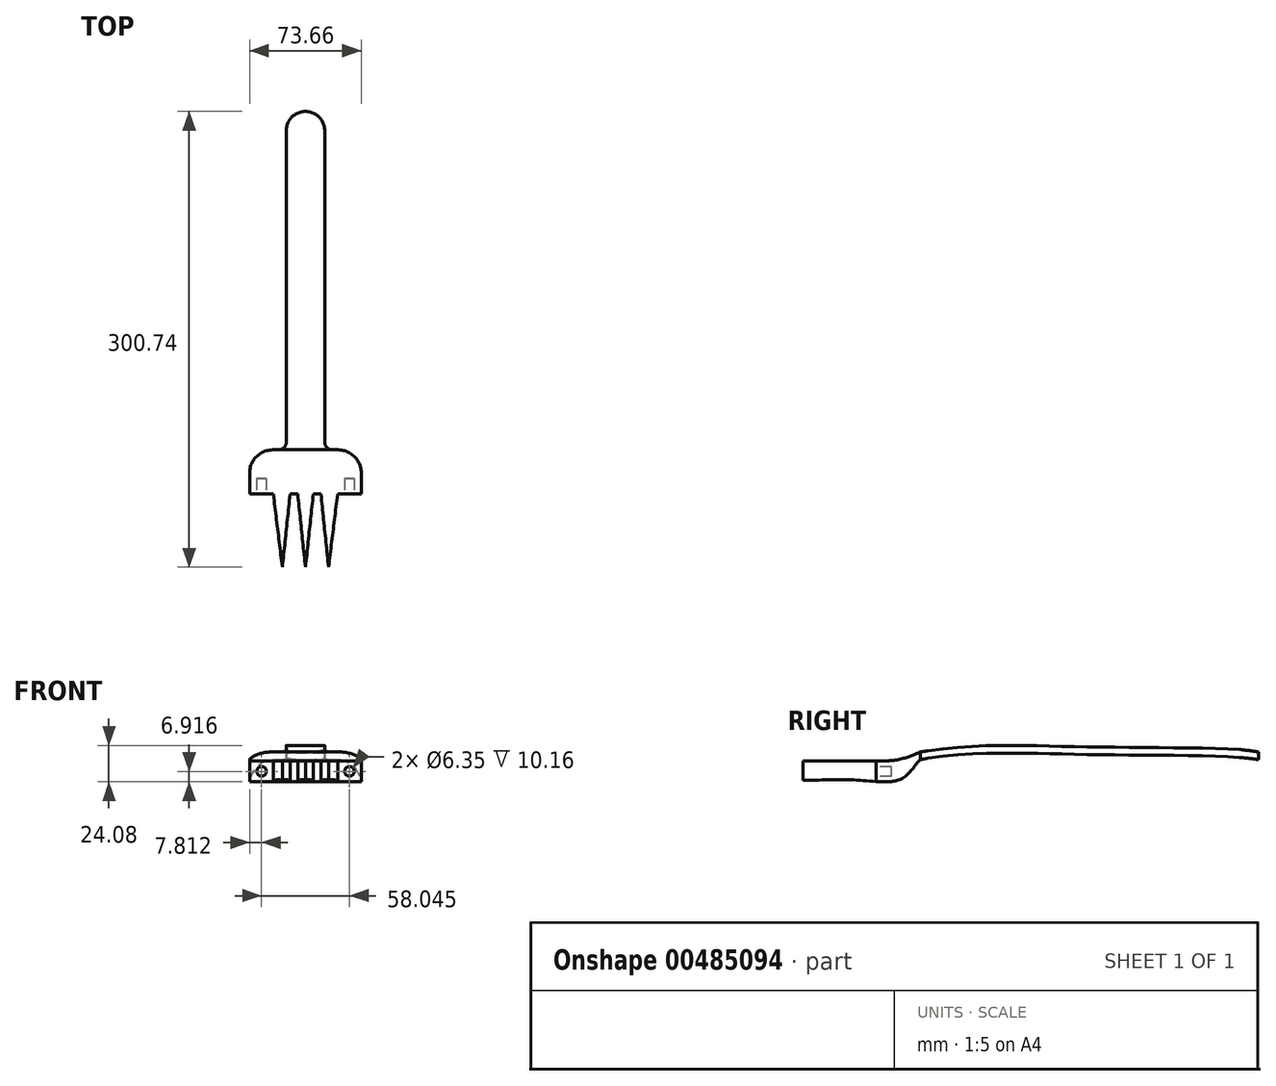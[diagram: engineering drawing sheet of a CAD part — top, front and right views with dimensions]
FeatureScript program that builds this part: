
annotation { "Feature Type Name" : "Feature", "Feature Type Description" : "" }
export const myFeature = defineFeature(function(context is Context, id is Id, definition is map)
    precondition{}
    {
        {
            var Q0;
            Q0=qCreatedBy(makeId("Top.planeOp"),FACE);
            var sketch = newSketch(context, id + "F0", { "sketchPlane" : qUnion([Q0])});
            skLineSegment(sketch, "E0", {"start": v(42, 63.5) * mm, "end": v(42, 0) * mm, "construction": true});
            skPoint(sketch, "E1", {"position": v(26.74, 8.89) * mm});
            skPoint(sketch, "E2", {"position": v(42, 8.89) * mm});
            skLineSegment(sketch, "E3", {"start": v(26.74, 8.89) * mm, "end": v(20.78, 57.15) * mm});
            skLineSegment(sketch, "E4", {"start": v(26.74, 8.89) * mm, "end": v(31.81, 57.15) * mm});
            skLineSegment(sketch, "E5", {"start": v(12.9, 57.15) * mm, "end": v(20.78, 57.15) * mm});
            skLineSegment(sketch, "E6", {"start": v(31.81, 57.15) * mm, "end": v(36.86, 57.15) * mm});
            skLineSegment(sketch, "E7", {"start": v(36.86, 57.15) * mm, "end": v(42, 8.89) * mm});
            skLineSegment(sketch, "E8.MirrorCS", {"start": v(47.13, 57.15) * mm, "end": v(42, 8.89) * mm});
            skPoint(sketch, "E9.MirrorP", {"position": v(57.24, 8.89) * mm});
            skLineSegment(sketch, "E10.MirrorCS", {"start": v(52.18, 57.15) * mm, "end": v(47.13, 57.15) * mm});
            skLineSegment(sketch, "E11.MirrorCS", {"start": v(71.1, 57.15) * mm, "end": v(63.2, 57.15) * mm});
            skLineSegment(sketch, "E12.MirrorCS", {"start": v(57.24, 8.89) * mm, "end": v(52.18, 57.15) * mm});
            skLineSegment(sketch, "E13.MirrorCS", {"start": v(57.24, 8.89) * mm, "end": v(63.2, 57.15) * mm});
            skLineSegment(sketch, "E14", {"start": v(12.9, 57.15) * mm, "end": v(12.9, 6.35) * mm});
            skLineSegment(sketch, "E15", {"start": v(12.9, 6.35) * mm, "end": v(18.85, 6.35) * mm});
            skLineSegment(sketch, "E16", {"start": v(18.85, 6.35) * mm, "end": v(18.85, 1.96) * mm});
            skLineSegment(sketch, "E17", {"start": v(18.85, 1.96) * mm, "end": v(5.16, 1.96) * mm});
            skLineSegment(sketch, "E18", {"start": v(5.16, 1.96) * mm, "end": v(5.16, 57.15) * mm});
            skLineSegment(sketch, "E19.MirrorCS", {"start": v(65.14, 6.35) * mm, "end": v(65.14, 1.96) * mm});
            skLineSegment(sketch, "E20.MirrorCS", {"start": v(71.1, 6.35) * mm, "end": v(65.14, 6.35) * mm});
            skLineSegment(sketch, "E21.MirrorCS", {"start": v(65.14, 1.96) * mm, "end": v(78.82, 1.96) * mm});
            skLineSegment(sketch, "E22.MirrorCS", {"start": v(71.1, 57.15) * mm, "end": v(71.1, 6.35) * mm});
            skLineSegment(sketch, "E23.MirrorCS", {"start": v(78.82, 1.96) * mm, "end": v(78.82, 57.15) * mm});
            skLineSegment(sketch, "E24", {"start": v(5.16, 57.15) * mm, "end": v(5.16, 63.5) * mm});
            skLineSegment(sketch, "E25", {"start": v(78.82, 57.15) * mm, "end": v(78.82, 63.5) * mm});
            skPoint(sketch, "E26.left.start.orphan", {"position": v(0, 0) * mm});
            skPoint(sketch, "E27.orphan", {"position": v(84.1, 63.5) * mm});
            skLineSegment(sketch, "E28.top", {"start": v(5.16, 86.36) * mm, "end": v(29.3, 86.36) * mm});
            skLineSegment(sketch, "E28.left", {"start": v(5.16, 63.5) * mm, "end": v(5.16, 86.36) * mm});
            skLineSegment(sketch, "E28.right", {"start": v(78.82, 63.5) * mm, "end": v(78.82, 86.36) * mm});
            skLineSegment(sketch, "E29.top", {"start": v(29.3, 309.63) * mm, "end": v(54.7, 309.63) * mm});
            skLineSegment(sketch, "E29.left", {"start": v(29.3, 86.36) * mm, "end": v(29.3, 309.63) * mm});
            skLineSegment(sketch, "E29.right", {"start": v(54.7, 86.36) * mm, "end": v(54.7, 309.63) * mm});
            skLineSegment(sketch, "E30.trimOffspring", {"start": v(54.7, 86.36) * mm, "end": v(78.82, 86.36) * mm});
            skSolve(sketch);
        }
        {
            var Q0;
            Q0=makeQuery(id+"F0.imprint","IMPRINT",FACE,{"disambiguationData":[TD([[makeQuery(id+"F0.imprint","IMPRINT",EDGE,{"derivedFrom":sQuery(id+"F0.wireOp",EDGE,"E3")}),-1.0]])]});
            extrude(context, id + "F1", {"entities" : qUnion([Q0]), "depth" : 101.6 * mm});
        }
        {
            var Q0;
            Q0=makeQuery(id+"F1.opExtrude","SWEPT_FACE",FACE,{"disambiguationData":[OSD([sQuery(id+"F0.wireOp",EDGE,"E29.right")])]});
            var sketch = newSketch(context, id + "F2", { "sketchPlane" : qUnion([Q0])});
            skLineSegment(sketch, "E31.0", {"start": v(86.36, 101.6) * mm, "end": v(86.36, 50.8) * mm});
            skLineSegment(sketch, "E31.1", {"start": v(86.36, 101.6) * mm, "end": v(309.63, 101.6) * mm});
            skLineSegment(sketch, "E31.2", {"start": v(309.63, 101.6) * mm, "end": v(309.63, 50.8) * mm});
            skLineSegment(sketch, "E31.3", {"start": v(86.36, 0) * mm, "end": v(309.63, 0) * mm});
            skFitSpline(sketch, "E32", {"points": [v(309.63, 50.8) * mm, v(274.25, 53.34) * mm, v(221.31, 53.85) * mm, v(176.46, 54.61) * mm, v(137.88, 55.12) * mm, v(86.36, 50.8) * mm], "startDerivative": vector(-185.69, 32.31) * mm, "endDerivative": vector(-247.75, -43.39) * mm});
            skFitSpline(sketch, "E33", {"points": [v(309.63, 45.72) * mm, v(274.25, 48.26) * mm, v(220.87, 48.77) * mm, v(176.9, 49.53) * mm, v(139.22, 50.04) * mm, v(86.36, 45.72) * mm], "startDerivative": vector(-185.5, 29.48) * mm, "endDerivative": vector(-251.8, -52.09) * mm});
            skLineSegment(sketch, "E34.trimOffspring", {"start": v(86.36, 45.72) * mm, "end": v(86.36, 0) * mm});
            skLineSegment(sketch, "E35.trimOffspring", {"start": v(309.63, 45.72) * mm, "end": v(309.63, 0) * mm});
            skSolve(sketch);
        }
        {
            var Q0;
            Q0=makeQuery(id+"F2.imprint","IMPRINT",FACE,{"disambiguationData":[TD([[makeQuery(id+"F2.imprint","IMPRINT",EDGE,{"derivedFrom":sQuery(id+"F2.wireOp",EDGE,"E31.3")}),1.0]])]});
            var Q1;
            Q1=makeQuery(id+"F2.imprint","IMPRINT",FACE,{"disambiguationData":[TD([[makeQuery(id+"F2.imprint","IMPRINT",EDGE,{"derivedFrom":sQuery(id+"F2.wireOp",EDGE,"E31.0")}),1.0]])]});
            extrude(context, id + "F3", {"entities" : qUnion([Q0, Q1]), "operationType" : NewBodyOperationType.REMOVE, "oppositeDirection" : true, "depth" : 25.4 * mm});
        }
        {
            var Q0;
            Q0=makeQuery(id+"F1.opExtrude","SWEPT_FACE",FACE,{"disambiguationData":[OSD([sQuery(id+"F0.wireOp",EDGE,"E23.MirrorCS"),sQuery(id+"F0.wireOp",EDGE,"E25"),sQuery(id+"F0.wireOp",EDGE,"E28.right")])]});
            var sketch = newSketch(context, id + "F4", { "sketchPlane" : qUnion([Q0])});
            skLineSegment(sketch, "E36.0", {"start": v(86.36, 101.6) * mm, "end": v(86.36, 50.8) * mm});
            skPoint(sketch, "E37.0", {"position": v(44.16, 101.6) * mm});
            skLineSegment(sketch, "E38.0", {"start": v(1.96, 101.6) * mm, "end": v(86.36, 101.6) * mm});
            skLineSegment(sketch, "E39.0", {"start": v(1.96, 101.6) * mm, "end": v(1.96, 44.74) * mm});
            skLineSegment(sketch, "E40.0", {"start": v(1.96, 0) * mm, "end": v(86.36, 0) * mm});
            skFitSpline(sketch, "E41.0", {"points": [v(309.63, 50.8) * mm, v(298.57, 52.72) * mm, v(273.86, 53.58) * mm, v(221.2, 53.72) * mm, v(176.6, 54.51) * mm, v(137.55, 55.75) * mm, v(104.18, 53.92) * mm, v(86.36, 50.8) * mm]});
            skFitSpline(sketch, "E42.0", {"points": [v(309.63, 45.72) * mm, v(298.57, 47.48) * mm, v(273.9, 48.6) * mm, v(220.8, 48.59) * mm, v(177.03, 49.51) * mm, v(138.84, 50.4) * mm, v(104.7, 49.52) * mm, v(86.36, 45.72) * mm]});
            skFitSpline(sketch, "E43", {"points": [v(86.36, 45.72) * mm, v(74.43, 33.37) * mm, v(44.15, 32.24) * mm, v(1.96, 32.04) * mm], "startDerivative": vector(-42.52, -37.37) * mm, "endDerivative": vector(-105.76, 0.67) * mm});
            skFitSpline(sketch, "E44", {"points": [v(86.36, 50.8) * mm, v(71.49, 45.72) * mm, v(43.42, 44.94) * mm, v(1.96, 44.74) * mm], "startDerivative": vector(-54.11, -21.48) * mm, "endDerivative": vector(-106.87, 0.66) * mm});
            skLineSegment(sketch, "E45.trimOffspring", {"start": v(1.96, 32.04) * mm, "end": v(1.96, 0) * mm});
            skLineSegment(sketch, "E46.trimOffspring", {"start": v(86.36, 45.72) * mm, "end": v(86.36, 0) * mm});
            skSolve(sketch);
        }
        {
            var Q0;
            Q0=qSketchRegion(id+"F4",true);
            extrude(context, id + "F5", {"entities" : qUnion([Q0]), "operationType" : NewBodyOperationType.REMOVE, "endBound" : BoundingType.THROUGH_ALL, "oppositeDirection" : true, "depth" : 25.4 * mm});
        }
        {
            var Q0;
            Q0=qCreatedBy(makeId("Top.planeOp"),FACE);
            var sketch = newSketch(context, id + "F6", { "sketchPlane" : qUnion([Q0])});
            skFitSpline(sketch, "E47.0", {"points": [v(5.16, 1.96) * mm, v(5.16, 16.57) * mm, v(5.16, 42.09) * mm, v(5.16, 71.13) * mm, v(5.16, 81.8) * mm, v(5.16, 86.36) * mm]});
            skLineSegment(sketch, "E47.1", {"start": v(5.16, 86.36) * mm, "end": v(12.9, 86.36) * mm});
            skLineSegment(sketch, "E47.5", {"start": v(5.16, 1.96) * mm, "end": v(18.85, 1.96) * mm});
            skFitSpline(sketch, "E47.6", {"points": [v(12.9, 86.36) * mm, v(12.9, 81.8) * mm, v(12.9, 71.13) * mm, v(12.9, 42.09) * mm, v(12.9, 16.57) * mm, v(12.9, 1.96) * mm]});
            skLineSegment(sketch, "E47.7", {"start": v(12.9, 6.35) * mm, "end": v(18.85, 6.35) * mm});
            skFitSpline(sketch, "E47.8", {"points": [v(18.85, 86.36) * mm, v(18.85, 81.8) * mm, v(18.85, 71.13) * mm, v(18.85, 42.09) * mm, v(18.85, 16.57) * mm, v(18.85, 1.96) * mm]});
            skPoint(sketch, "E47.12", {"position": v(12, 1.96) * mm});
            skLineSegment(sketch, "E48", {"start": v(12.9, 57.15) * mm, "end": v(12.9, 86.36) * mm});
            skPoint(sketch, "E49.orphan", {"position": v(29.3, 86.36) * mm});
            skPoint(sketch, "E50.orphan", {"position": v(54.7, 86.36) * mm});
            skPoint(sketch, "E47.3.start.orphan", {"position": v(78.82, 86.36) * mm});
            skPoint(sketch, "E47.4.end.orphan", {"position": v(78.82, 1.96) * mm});
            skPoint(sketch, "E47.9.end.orphan", {"position": v(65.14, 1.96) * mm});
            skPoint(sketch, "E47.10.end.orphan", {"position": v(65.14, 6.35) * mm});
            skPoint(sketch, "E47.11.end.orphan", {"position": v(71.1, 6.35) * mm});
            skPoint(sketch, "E47.11.start.orphan", {"position": v(71.1, 57.15) * mm});
            skSolve(sketch);
        }
        {
            var Q0;
            Q0=qCreatedBy(makeId("Top.planeOp"),FACE);
            var sketch = newSketch(context, id + "F7", { "sketchPlane" : qUnion([Q0])});
            skLineSegment(sketch, "E51.0", {"start": v(54.7, 86.36) * mm, "end": v(78.82, 86.36) * mm});
            skFitSpline(sketch, "E52.0", {"points": [v(78.82, 86.36) * mm, v(78.82, 81.8) * mm, v(78.82, 71.13) * mm, v(78.82, 42.09) * mm, v(78.82, 16.57) * mm, v(78.82, 1.96) * mm]});
            skLineSegment(sketch, "E53.0", {"start": v(65.14, 1.96) * mm, "end": v(78.82, 1.96) * mm});
            skFitSpline(sketch, "E54.0", {"points": [v(5.16, 1.96) * mm, v(5.16, 16.57) * mm, v(5.16, 42.09) * mm, v(5.16, 71.13) * mm, v(5.16, 81.8) * mm, v(5.16, 86.36) * mm]});
            skLineSegment(sketch, "E55.0", {"start": v(5.16, 86.36) * mm, "end": v(12.9, 86.36) * mm});
            skLineSegment(sketch, "E56.0", {"start": v(5.16, 86.36) * mm, "end": v(29.3, 86.36) * mm});
            skFitSpline(sketch, "E57.0", {"points": [v(12.9, 86.36) * mm, v(12.9, 81.8) * mm, v(12.9, 71.13) * mm, v(12.9, 42.09) * mm, v(12.9, 16.57) * mm, v(12.9, 1.96) * mm]});
            skFitSpline(sketch, "E58", {"points": [v(5.16, 68.65) * mm, v(7.16, 73.06) * mm, v(10.75, 78.13) * mm, v(15, 83.52) * mm, v(18.92, 86.36) * mm], "startDerivative": vector(7.41, 19.15) * mm, "endDerivative": vector(17.3, 10.48) * mm});
            skLineSegment(sketch, "E59.0", {"start": v(29.3, 86.36) * mm, "end": v(54.7, 86.36) * mm});
            skLineSegment(sketch, "E60", {"start": v(5.16, 68.65) * mm, "end": v(5.16, 86.36) * mm});
            skSolve(sketch);
        }
        {
            var Q0;
            Q0=qCreatedBy(makeId("Top.planeOp"),FACE);
            cPlane(context, id + "F8", {"entities" : qUnion([Q0]), "cplaneType" : CPlaneType.OFFSET, "offset" : 50.8 * mm, "width" : 152.4 * mm, "height" : 152.4 * mm});
        }
        {
            var Q0;
            Q0=qCreatedBy(id+"F8.planeOp",FACE);
            var sketch = newSketch(context, id + "F9", { "sketchPlane" : qUnion([Q0])});
            skFitSpline(sketch, "E61.0", {"points": [v(5.16, 1.96) * mm, v(5.16, 16.57) * mm, v(5.16, 42.09) * mm, v(5.16, 71.13) * mm, v(5.16, 81.8) * mm, v(5.16, 86.36) * mm]});
            skLineSegment(sketch, "E62.0", {"start": v(5.16, 1.96) * mm, "end": v(18.85, 1.96) * mm});
            skFitSpline(sketch, "E63.0", {"points": [v(18.85, 86.36) * mm, v(18.85, 81.8) * mm, v(18.85, 71.13) * mm, v(18.85, 42.09) * mm, v(18.85, 16.57) * mm, v(18.85, 1.96) * mm]});
            skLineSegment(sketch, "E64.0", {"start": v(12.9, 6.35) * mm, "end": v(18.85, 6.35) * mm});
            skFitSpline(sketch, "E65.0", {"points": [v(12.9, 86.36) * mm, v(12.9, 81.8) * mm, v(12.9, 71.13) * mm, v(12.9, 42.09) * mm, v(12.9, 16.57) * mm, v(12.9, 1.96) * mm]});
            skLineSegment(sketch, "E66", {"start": v(12.9, 57.15) * mm, "end": v(5.16, 57.15) * mm});
            skPoint(sketch, "E67.orphan", {"position": v(5.16, 86.36) * mm});
            skSolve(sketch);
        }
        {
            var Q0;
            Q0=qSketchRegion(id+"F9",true);
            extrude(context, id + "F10", {"entities" : qUnion([Q0]), "operationType" : NewBodyOperationType.REMOVE, "endBound" : BoundingType.THROUGH_ALL, "oppositeDirection" : true, "depth" : 16.5 * mm});
        }
        {
            var Q0;
            Q0=qCreatedBy(makeId("Top.planeOp"),FACE);
            cPlane(context, id + "F11", {"entities" : qUnion([Q0]), "cplaneType" : CPlaneType.OFFSET, "offset" : 30.48 * mm, "width" : 152.4 * mm, "height" : 152.4 * mm});
        }
        {
            var Q0;
            Q0=qCreatedBy(id+"F11.planeOp",FACE);
            var sketch = newSketch(context, id + "F12", { "sketchPlane" : qUnion([Q0])});
            skFitSpline(sketch, "E68.0", {"points": [v(71.1, 86.36) * mm, v(71.1, 81.8) * mm, v(71.1, 71.13) * mm, v(71.1, 42.09) * mm, v(71.1, 16.57) * mm, v(71.1, 1.96) * mm]});
            skLineSegment(sketch, "E69.0", {"start": v(65.14, 1.96) * mm, "end": v(78.82, 1.96) * mm});
            skLineSegment(sketch, "E70.0", {"start": v(71.1, 6.35) * mm, "end": v(65.14, 6.35) * mm});
            skFitSpline(sketch, "E71.0", {"points": [v(65.14, 86.36) * mm, v(65.14, 81.8) * mm, v(65.14, 71.13) * mm, v(65.14, 42.09) * mm, v(65.14, 16.57) * mm, v(65.14, 1.96) * mm]});
            skFitSpline(sketch, "E72.0", {"points": [v(78.82, 86.36) * mm, v(78.82, 81.8) * mm, v(78.82, 71.13) * mm, v(78.82, 42.09) * mm, v(78.82, 16.57) * mm, v(78.82, 1.96) * mm]});
            skLineSegment(sketch, "E73", {"start": v(71.1, 57.15) * mm, "end": v(78.82, 57.15) * mm});
            skPoint(sketch, "E74.orphan", {"position": v(78.82, 86.36) * mm});
            skSolve(sketch);
        }
        {
            var Q0;
            Q0=qSketchRegion(id+"F12",true);
            extrude(context, id + "F13", {"entities" : qUnion([Q0]), "operationType" : NewBodyOperationType.REMOVE, "depth" : 11.43 * mm});
        }
        {
            var Q0;
            Q0=qSketchRegion(id+"F7",true);
            extrude(context, id + "F14", {"entities" : qUnion([Q0]), "operationType" : NewBodyOperationType.REMOVE, "oppositeDirection" : true, "depth" : 25.4 * mm});
        }
        {
            var Q0;
            Q0=makeQuery(id+"F1.opExtrude","SWEPT_EDGE",EDGE,{"disambiguationData":[OSD([sQuery(id+"F0.wireOp",EDGE,"E28.right"),sQuery(id+"F0.wireOp",EDGE,"E30.trimOffspring")])]});
            fillet(context, id + "F15", {"entities" : qUnion([Q0]), "radius" : 15.24 * mm, "tangentPropagation" : true, "allowEdgeOverflow" : false});
        }
        {
            var Q0;
            Q0=makeQuery(id+"F1.opExtrude","SWEPT_EDGE",EDGE,{"disambiguationData":[OSD([sQuery(id+"F0.wireOp",EDGE,"E28.top"),sQuery(id+"F0.wireOp",EDGE,"E28.left")])]});
            fillet(context, id + "F16", {"entities" : qUnion([Q0]), "radius" : 15.24 * mm, "tangentPropagation" : true, "allowEdgeOverflow" : false});
        }
        {
            var Q0;
            Q0=makeQuery(id+"F1.opExtrude","SWEPT_EDGE",EDGE,{"disambiguationData":[OSD([sQuery(id+"F0.wireOp",EDGE,"E28.top"),sQuery(id+"F0.wireOp",EDGE,"E29.left")])]});
            fillet(context, id + "F17", {"entities" : qUnion([Q0]), "radius" : 5.08 * mm, "tangentPropagation" : true, "allowEdgeOverflow" : false});
        }
        {
            var Q0;
            Q0=makeQuery(id+"F1.opExtrude","SWEPT_EDGE",EDGE,{"disambiguationData":[OSD([sQuery(id+"F0.wireOp",EDGE,"E29.right"),sQuery(id+"F0.wireOp",EDGE,"E30.trimOffspring")])]});
            fillet(context, id + "F18", {"entities" : qUnion([Q0]), "radius" : 5.08 * mm, "tangentPropagation" : true, "allowEdgeOverflow" : false});
        }
        {
            var Q0;
            Q0=makeQuery(id+"F1.opExtrude","SWEPT_EDGE",EDGE,{"disambiguationData":[OSD([sQuery(id+"F0.wireOp",EDGE,"E29.top"),sQuery(id+"F0.wireOp",EDGE,"E29.right")])]});
            var Q1;
            Q1=makeQuery(id+"F1.opExtrude","SWEPT_EDGE",EDGE,{"disambiguationData":[OSD([sQuery(id+"F0.wireOp",EDGE,"E29.top"),sQuery(id+"F0.wireOp",EDGE,"E29.left")])]});
            fillet(context, id + "F19", {"entities" : qUnion([Q0, Q1]), "radius" : 12.7 * mm, "tangentPropagation" : true, "allowEdgeOverflow" : false});
        }
        {
            var Q0;
            Q0=qCreatedBy(id+"F11.planeOp",FACE);
            var sketch = newSketch(context, id + "F20", { "sketchPlane" : qUnion([Q0])});
            skLineSegment(sketch, "E75.0", {"start": v(5.16, 1.96) * mm, "end": v(18.85, 1.96) * mm});
            skFitSpline(sketch, "E76.0", {"points": [v(5.16, 1.96) * mm, v(5.16, 16.57) * mm, v(5.16, 42.09) * mm, v(5.16, 71.13) * mm, v(5.16, 81.8) * mm, v(5.16, 86.36) * mm]});
            skFitSpline(sketch, "E77.0", {"points": [v(12.9, 86.36) * mm, v(12.9, 81.8) * mm, v(12.9, 71.13) * mm, v(12.9, 42.09) * mm, v(12.9, 16.57) * mm, v(12.9, 1.96) * mm]});
            skLineSegment(sketch, "E78.0", {"start": v(12.9, 6.35) * mm, "end": v(18.85, 6.35) * mm});
            skFitSpline(sketch, "E79.0", {"points": [v(71.1, 86.36) * mm, v(71.1, 81.8) * mm, v(71.1, 71.13) * mm, v(71.1, 42.09) * mm, v(71.1, 16.57) * mm, v(71.1, 1.96) * mm]});
            skPoint(sketch, "E80.0", {"position": v(68.12, 6.35) * mm});
            skLineSegment(sketch, "E81.0", {"start": v(71.1, 6.35) * mm, "end": v(65.14, 6.35) * mm});
            skFitSpline(sketch, "E82.0", {"points": [v(65.14, 86.36) * mm, v(65.14, 81.8) * mm, v(65.14, 71.13) * mm, v(65.14, 42.09) * mm, v(65.14, 16.57) * mm, v(65.14, 1.96) * mm]});
            skLineSegment(sketch, "E83.0", {"start": v(65.14, 1.96) * mm, "end": v(78.82, 1.96) * mm});
            skFitSpline(sketch, "E84.0", {"points": [v(78.82, 86.36) * mm, v(78.82, 81.8) * mm, v(78.82, 71.13) * mm, v(78.82, 42.09) * mm, v(78.82, 16.57) * mm, v(78.82, 1.96) * mm]});
            skLineSegment(sketch, "E85", {"start": v(12.9, 57.15) * mm, "end": v(5.16, 57.15) * mm});
            skLineSegment(sketch, "E86", {"start": v(71.1, 57.15) * mm, "end": v(78.82, 57.15) * mm});
            skSolve(sketch);
        }
        {
            var Q0;
            Q0 = qSketchRegion(id + "F20", true);
            extrude(context, id + "F21", {"entities" : qUnion([Q0]), "operationType" : NewBodyOperationType.REMOVE, "endBound" : BoundingType.THROUGH_ALL, "depth" : 25.4 * mm});
        }
        {
            var Q0;
            Q0=makeQuery(id+"F21.boolean.opBoolean","MERGE",FACE,{"derivedFrom":[makeQuery(id+"F13.boolean.opBoolean","MERGE",FACE,{"derivedFrom":[makeQuery(id+"F1.opExtrude","SWEPT_FACE",FACE,{"disambiguationData":[OSD([sQuery(id+"F0.wireOp",EDGE,"E11.MirrorCS")])]}),makeQuery(id+"F13.opExtrude","SWEPT_FACE",FACE,{"disambiguationData":[OSD([sQuery(id+"F12.wireOp",EDGE,"E73")])]})]}),makeQuery(id+"F21.opExtrude","SWEPT_FACE",FACE,{"disambiguationData":[OSD([sQuery(id+"F20.wireOp",EDGE,"E86")])]})]});
            var sketch = newSketch(context, id + "F22", { "sketchPlane" : qUnion([Q0])});
            skCircle(sketch, "E87", {"center": v(12.97, 38) * mm, "radius": 3.18 * mm});
            skCircle(sketch, "E88.MirrorC", {"center": v(71.02, 38) * mm, "radius": 3.18 * mm});
            skSolve(sketch);
        }
        {
            var Q0;
            Q0 = qSketchRegion(id + "F22", true);
            extrude(context, id + "F23", {"entities" : qUnion([Q0]), "operationType" : NewBodyOperationType.REMOVE, "oppositeDirection" : true, "depth" : 10.16 * mm});
        }
    });
